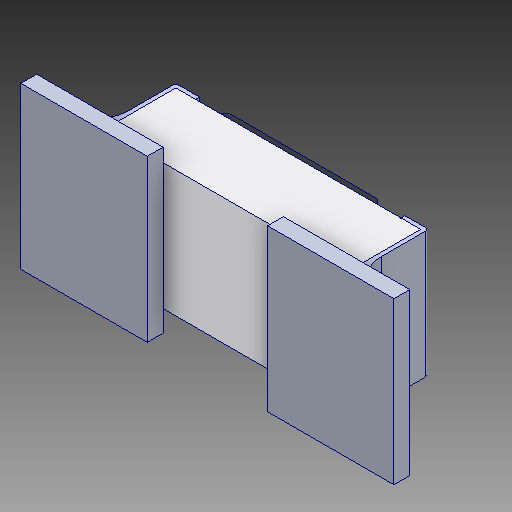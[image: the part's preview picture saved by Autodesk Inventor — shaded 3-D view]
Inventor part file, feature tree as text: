
AUTODESK INVENTOR PART (.ipt)
format: ipt  version: 2018 (Build 220112000, 112)  size: 218,112 bytes
history: native  units: mm
features: other x2, fillet x2
ambient origin geometry x8: Origin, YZ Plane, XZ Plane, XY Plane, X Axis, Y Axis, Z Axis, Center Point
bodies: Volumenkörper1 (feature_tree), Volumenkörper2 (feature_tree), Volumenkörper3 (feature_tree), Volumenkörper4 (feature_tree)
feature tree (4):
  other  "Boss-Extrude1"
  other  "Boss-Extrude4"
  fillet  "Fillet6"  [1 undecoded]
  fillet  "Fillet5"  [1 undecoded]
note: 2 required parameter values undecoded (feature->parameter linkage not recoverable at this tier; creation-order binding heuristic only, values carry confidence <= 0.55)
